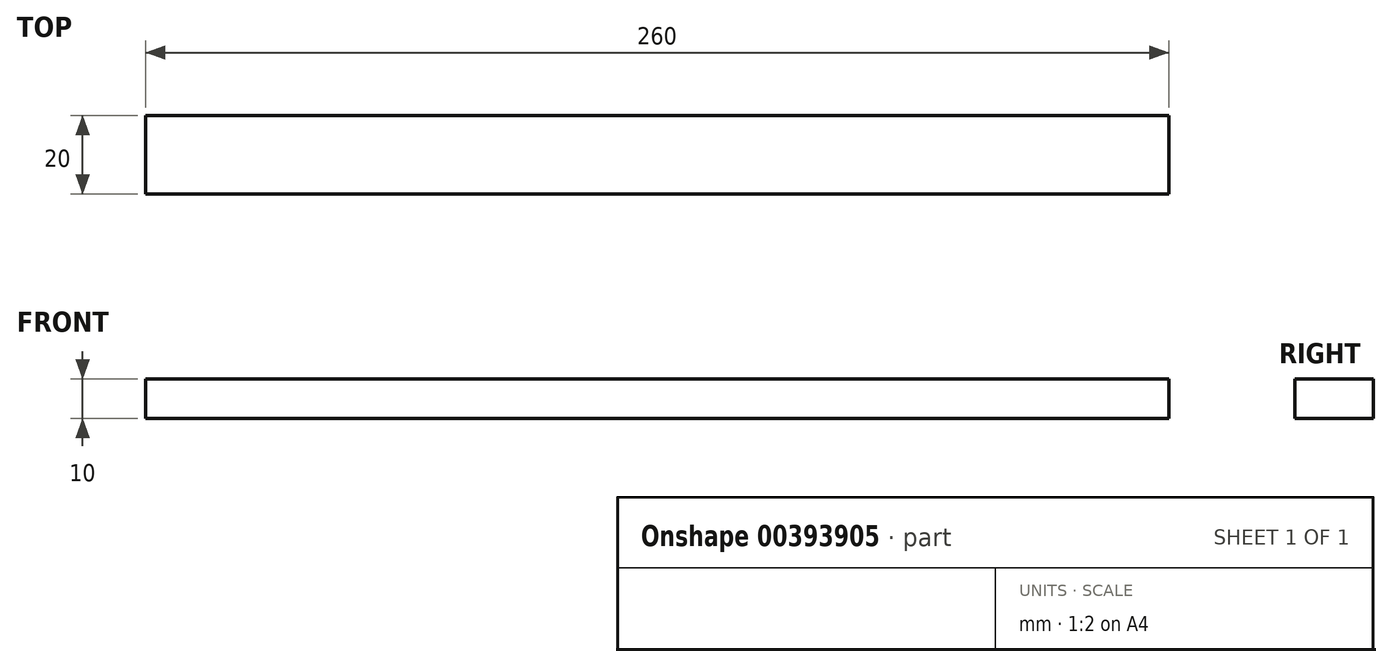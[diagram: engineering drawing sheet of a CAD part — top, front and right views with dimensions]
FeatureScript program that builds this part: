
annotation { "Feature Type Name" : "Feature", "Feature Type Description" : "" }
export const myFeature = defineFeature(function(context is Context, id is Id, definition is map)
    precondition{}
    {
        {
            var Q0;
            Q0=qCreatedBy(makeId("Front.planeOp"),FACE);
            var sketch = newSketch(context, id + "F0", { "sketchPlane" : qUnion([Q0])});
            skLineSegment(sketch, "E0.bottom", {"start": v(130, 5) * mm, "end": v(-130, 5) * mm});
            skLineSegment(sketch, "E0.top", {"start": v(130, -5) * mm, "end": v(-130, -5) * mm});
            skLineSegment(sketch, "E0.left", {"start": v(130, 5) * mm, "end": v(130, -5) * mm});
            skLineSegment(sketch, "E0.right", {"start": v(-130, 5) * mm, "end": v(-130, -5) * mm});
            skPoint(sketch, "E0.middle", {"position": v(0, 0) * mm});
            skSolve(sketch);
        }
        {
            var Q0;
            Q0=makeQuery(id+"F0.imprint","IMPRINT",FACE,{"disambiguationData":[TD([[makeQuery(id+"F0.imprint","IMPRINT",EDGE,{"derivedFrom":sQuery(id+"F0.wireOp",EDGE,"E0.bottom")}),1.0]])]});
            extrude(context, id + "F1", {"entities" : qUnion([Q0]), "depth" : 20 * mm, "offsetDistance" : 25 * mm});
        }
    });
